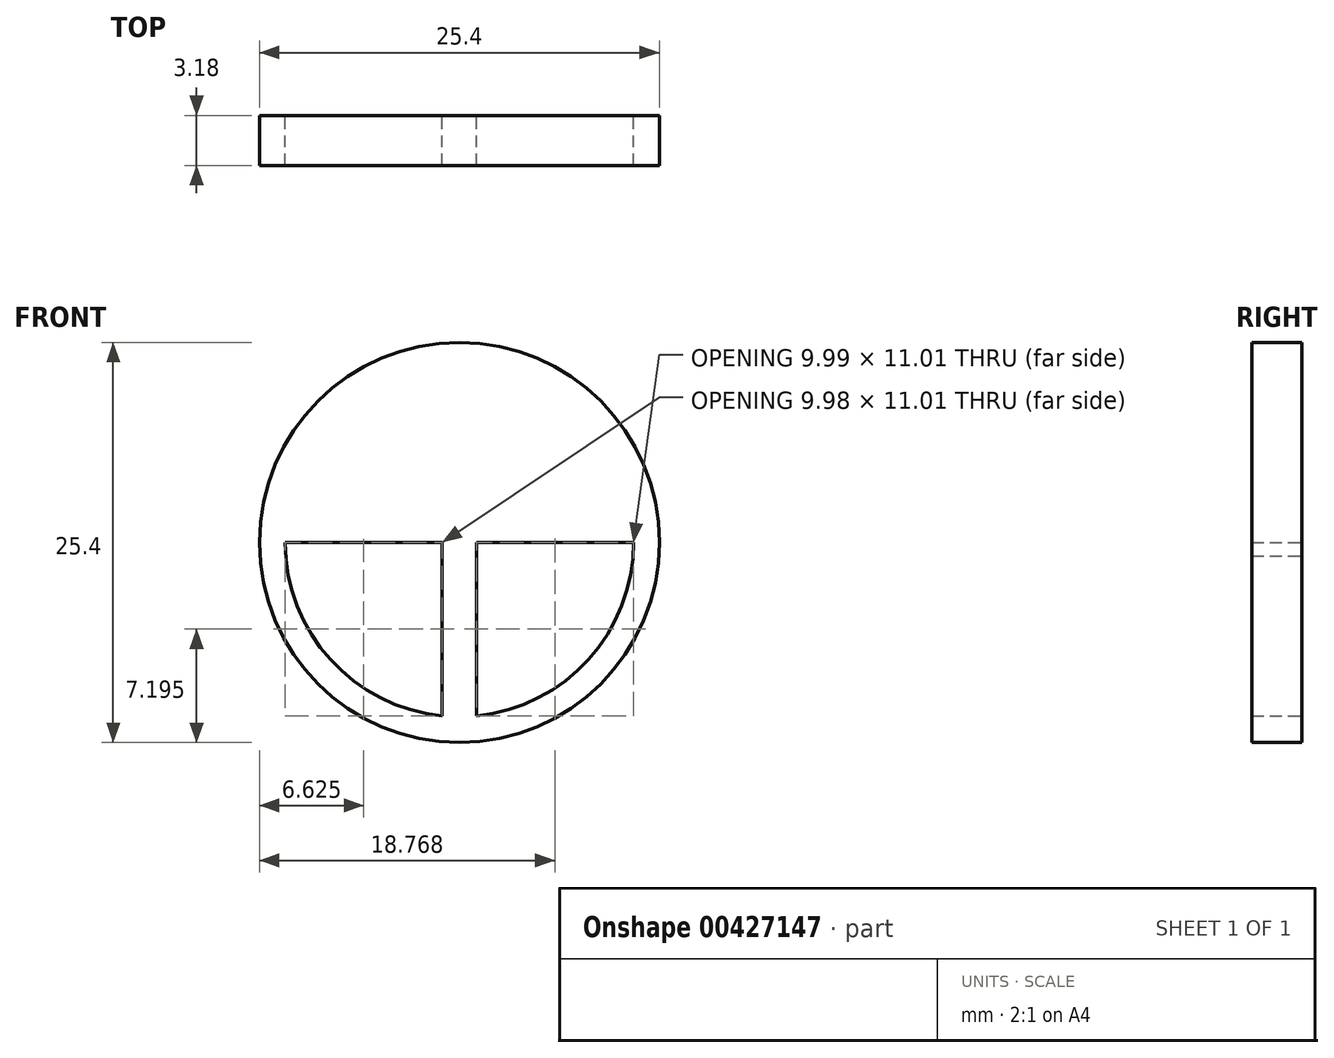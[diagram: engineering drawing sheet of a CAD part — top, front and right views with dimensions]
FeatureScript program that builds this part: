
annotation { "Feature Type Name" : "Feature", "Feature Type Description" : "" }
export const myFeature = defineFeature(function(context is Context, id is Id, definition is map)
    precondition{}
    {
        {
            var Q0;
            Q0=qCreatedBy(makeId("Front.planeOp"),FACE);
            var sketch = newSketch(context, id + "F0", { "sketchPlane" : qUnion([Q0])});
            skCircle(sketch, "E0", {"center": v(0, 0) * mm, "radius": 12.7 * mm});
            skCircle(sketch, "E1", {"center": v(0, 0) * mm, "radius": 11.06 * mm});
            skLineSegment(sketch, "E2", {"start": v(0, 9.46) * mm, "end": v(-1.09, 9.46) * mm});
            skLineSegment(sketch, "E3", {"start": v(-1.09, 9.46) * mm, "end": v(-1.09, 11) * mm});
            skLineSegment(sketch, "E4", {"start": v(0, 9.46) * mm, "end": v(1.09, 9.46) * mm});
            skLineSegment(sketch, "E5", {"start": v(1.09, 9.46) * mm, "end": v(1.09, 11) * mm});
            skLineSegment(sketch, "E6", {"start": v(-11.06, 0) * mm, "end": v(11.06, 0) * mm});
            skLineSegment(sketch, "E7", {"start": v(-11.03, -0.85) * mm, "end": v(11.03, -0.85) * mm});
            skLineSegment(sketch, "E8", {"start": v(0, -0.85) * mm, "end": v(-1.09, -0.85) * mm});
            skLineSegment(sketch, "E9", {"start": v(0, -0.85) * mm, "end": v(1.09, -0.85) * mm});
            skLineSegment(sketch, "E10", {"start": v(1.09, -0.85) * mm, "end": v(0, -0.85) * mm});
            skLineSegment(sketch, "E11", {"start": v(-0.57, -11.05) * mm, "end": v(-0.57, -0.85) * mm});
            skLineSegment(sketch, "E12", {"start": v(0.54, -0.85) * mm, "end": v(0.54, -11.05) * mm});
            skLineSegment(sketch, "E13", {"start": v(-0.57, -0.85) * mm, "end": v(-0.57, 0.86) * mm});
            skLineSegment(sketch, "E14", {"start": v(0.54, -0.85) * mm, "end": v(0.54, 0.86) * mm});
            skLineSegment(sketch, "E15", {"start": v(-0.57, 0.86) * mm, "end": v(-0.57, 1.32) * mm});
            skLineSegment(sketch, "E16", {"start": v(0.54, 0.86) * mm, "end": v(0.54, 1.32) * mm});
            skLineSegment(sketch, "E17", {"start": v(0.54, 1.32) * mm, "end": v(-0.57, 1.32) * mm});
            skLineSegment(sketch, "E18", {"start": v(-1.09, -0.85) * mm, "end": v(-1.09, -11) * mm});
            skLineSegment(sketch, "E19", {"start": v(1.09, -0.85) * mm, "end": v(1.09, -11) * mm});
            skLineSegment(sketch, "E20", {"start": v(-0.57, 1.32) * mm, "end": v(-1.09, 1.32) * mm});
            skLineSegment(sketch, "E21", {"start": v(-1.09, 1.32) * mm, "end": v(-1.09, -0.85) * mm});
            skLineSegment(sketch, "E22", {"start": v(0.54, 1.32) * mm, "end": v(1.05, 1.32) * mm});
            skLineSegment(sketch, "E23", {"start": v(1.05, 1.32) * mm, "end": v(1.09, -0.85) * mm});
            skSolve(sketch);
        }
        {
            var Q0;
            Q0=makeQuery(id+"F0.imprint","IMPRINT",FACE,{"disambiguationData":[TD([[makeQuery(id+"F0.imprint","IMPRINT",EDGE,{"derivedFrom":sQuery(id+"F0.wireOp",EDGE,"E0")}),1.0]])]});
            var Q1;
            Q1=makeQuery(id+"F0.imprint","IMPRINT",FACE,{"disambiguationData":[TD([[makeQuery(id+"F0.imprint","IMPRINT",EDGE,{"derivedFrom":sQuery(id+"F0.wireOp",EDGE,"E2")}),-1.0]])]});
            var Q2;
            {var subQ0=sQuery(id+"F0.wireOp",EDGE,"E6");var subQ1=sQuery(id+"F0.wireOp",EDGE,"E1");var subQ2=makeQuery(id+"F0.imprint","INTERSECT",VERTEX,{"disambiguationData":[OD(1.0)],"derivedFrom":[subQ1,subQ0]});Q2=makeQuery(id+"F0.imprint","IMPRINT",FACE,{"disambiguationData":[TD([[makeQuery(id+"F0.imprint","IMPRINT",EDGE,{"disambiguationData":[TD([[subQ2,1.0]])],"derivedFrom":subQ1}),1.0]])]});}
            var Q3;
            {var subQ0=sQuery(id+"F0.wireOp",EDGE,"E6");var subQ1=sQuery(id+"F0.wireOp",EDGE,"E1");var subQ2=makeQuery(id+"F0.imprint","INTERSECT",VERTEX,{"disambiguationData":[OD(0.0)],"derivedFrom":[subQ1,subQ0]});Q3=makeQuery(id+"F0.imprint","IMPRINT",FACE,{"disambiguationData":[TD([[makeQuery(id+"F0.imprint","IMPRINT",EDGE,{"disambiguationData":[TD([[subQ2,-1.0]])],"derivedFrom":subQ1}),1.0]])]});}
            var Q4;
            {var subQ1=sQuery(id+"F0.wireOp",EDGE,"E15");Q4=makeQuery(id+"F0.imprint","IMPRINT",FACE,{"disambiguationData":[TD([[makeQuery(id+"F0.imprint","IMPRINT",EDGE,{"derivedFrom":subQ1}),1.0]])]});}
            var Q5;
            {var subQ6=sQuery(id+"F0.wireOp",EDGE,"E16");Q5=makeQuery(id+"F0.imprint","IMPRINT",FACE,{"disambiguationData":[TD([[makeQuery(id+"F0.imprint","IMPRINT",EDGE,{"derivedFrom":subQ6}),-1.0]])]});}
            var Q6;
            {var subQ4=sQuery(id+"F0.wireOp",EDGE,"E15");Q6=makeQuery(id+"F0.imprint","IMPRINT",FACE,{"disambiguationData":[TD([[makeQuery(id+"F0.imprint","IMPRINT",EDGE,{"derivedFrom":subQ4}),-1.0]])]});}
            var Q7;
            {var subQ0=sQuery(id+"F0.wireOp",EDGE,"E13");var subQ3=sQuery(id+"F0.wireOp",EDGE,"E6");var subQ4=makeQuery(id+"F0.imprint","INTERSECT",VERTEX,{"derivedFrom":[subQ3,subQ0]});Q7=makeQuery(id+"F0.imprint","IMPRINT",FACE,{"disambiguationData":[TD([[makeQuery(id+"F0.imprint","IMPRINT",EDGE,{"disambiguationData":[TD([[subQ4,-1.0]])],"derivedFrom":subQ3}),-1.0]])]});}
            var Q8;
            {var subQ0=sQuery(id+"F0.wireOp",EDGE,"E21");var subQ1=sQuery(id+"F0.wireOp",EDGE,"E6");var subQ2=makeQuery(id+"F0.imprint","INTERSECT",VERTEX,{"derivedFrom":[subQ1,subQ0]});Q8=makeQuery(id+"F0.imprint","IMPRINT",FACE,{"disambiguationData":[TD([[makeQuery(id+"F0.imprint","IMPRINT",EDGE,{"disambiguationData":[TD([[subQ2,-1.0]])],"derivedFrom":subQ1}),-1.0]])]});}
            var Q9;
            {var subQ0=sQuery(id+"F0.wireOp",EDGE,"E14");var subQ1=sQuery(id+"F0.wireOp",EDGE,"E6");var subQ2=makeQuery(id+"F0.imprint","INTERSECT",VERTEX,{"derivedFrom":[subQ1,subQ0]});Q9=makeQuery(id+"F0.imprint","IMPRINT",FACE,{"disambiguationData":[TD([[makeQuery(id+"F0.imprint","IMPRINT",EDGE,{"disambiguationData":[TD([[subQ2,-1.0]])],"derivedFrom":subQ1}),-1.0]])]});}
            var Q10;
            {var subQ0=sQuery(id+"F0.wireOp",EDGE,"E11");Q10=makeQuery(id+"F0.imprint","IMPRINT",FACE,{"disambiguationData":[TD([[makeQuery(id+"F0.imprint","IMPRINT",EDGE,{"derivedFrom":subQ0}),1.0]])]});}
            var Q11;
            {var subQ0=sQuery(id+"F0.wireOp",EDGE,"E11");Q11=makeQuery(id+"F0.imprint","IMPRINT",FACE,{"disambiguationData":[TD([[makeQuery(id+"F0.imprint","IMPRINT",EDGE,{"derivedFrom":subQ0}),-1.0]])]});}
            var Q12;
            {var subQ0=sQuery(id+"F0.wireOp",EDGE,"E12");Q12=makeQuery(id+"F0.imprint","IMPRINT",FACE,{"disambiguationData":[TD([[makeQuery(id+"F0.imprint","IMPRINT",EDGE,{"derivedFrom":subQ0}),1.0]])]});}
            extrude(context, id + "F1", {"entities" : qUnion([Q0, Q1, Q2, Q3, Q4, Q5, Q6, Q7, Q8, Q9, Q10, Q11, Q12]), "depth" : 3.17 * mm});
        }
    });
